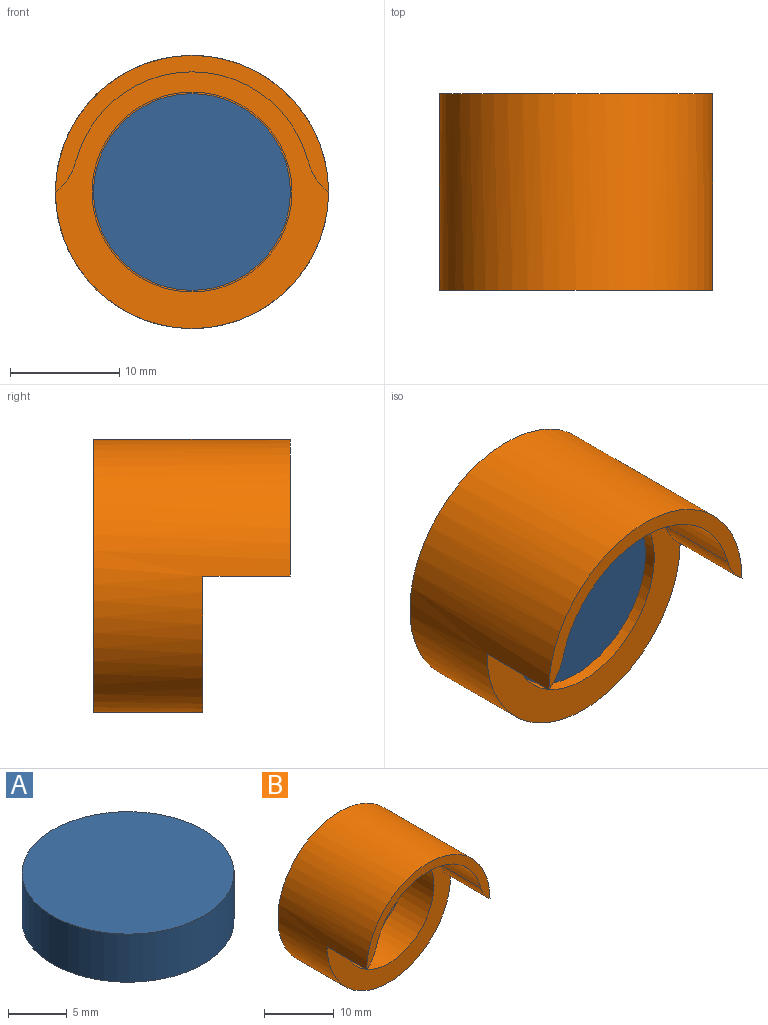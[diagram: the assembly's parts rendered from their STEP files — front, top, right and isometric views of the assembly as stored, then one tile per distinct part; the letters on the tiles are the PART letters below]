
ASSEMBLY  parts=2 mates=1
PART A: 3 faces, bbox 18x18x5 mm
  f0: cylinder r=9mm len=18mm, axis (0,0,-1), area 282.7mm2, adj f1,f2
  f1: plane 18x18mm, normal (0,0,1), area 254.5mm2, adj f0
  f2: plane 18x18mm, normal (0,0,-1), area 254.5mm2, adj f0
PART B: 13 faces, bbox 25x18x25 mm
  f0: plane 25x12.5mm, normal (0,-1,0), area 52.8mm2, adj f1,f3,f7,f8
  f1: cylinder r=12.5mm len=25mm, axis (0,1,0), area 1099.6mm2, adj f0,f2,f4,f7,f8
  f2: plane 25x25mm, normal (0,1,0), area 454.7mm2, adj f1,f9,f11
  f3: cylinder r=11mm len=21.3mm, axis (0,-1,0), area 231.9mm2, adj f0,f4,f7,f8
  f4: plane 25x23.5mm, normal (0,-1,0), area 175mm2, adj f1,f3,f5,f7,f8
  f5: cylinder r=9.15mm len=18.3mm, axis (0,-1,0), area 344.9mm2, adj f4,f6
  f6: plane 18.3x18.3mm, normal (0,-1,0), area 152.2mm2, adj f5,f10,f12
  f7: cylinder r=5mm len=8mm, axis (0,-1,0), area 27.1mm2, adj f0,f1,f3,f4
  f8: cylinder r=5mm len=8mm, axis (0,-1,0), area 27.1mm2, adj f0,f1,f3,f4
  f9: cylinder r=2.4mm len=4.8mm, axis (0,-1,0), area 15.1mm2, adj f2,f10
  f10: cone r=2.4mm half-angle=31deg, axis (0,-1,0), area 72.5mm2, adj f6,f9
  f11: cylinder r=2.4mm len=4.8mm, axis (0,-1,0), area 15.1mm2, adj f2,f12
  f12: cone r=4.2mm half-angle=31deg, axis (0,-1,0), area 72.5mm2, adj f6,f11
PLACE A rot(axis=(-1,0,0),90deg) t=(0,-11,0)mm
PLACE B t=(0,-2,0)mm
MATE fastened A.f0 <-> B.f1  axis (0,1,0) through (0,-6,0)mm
